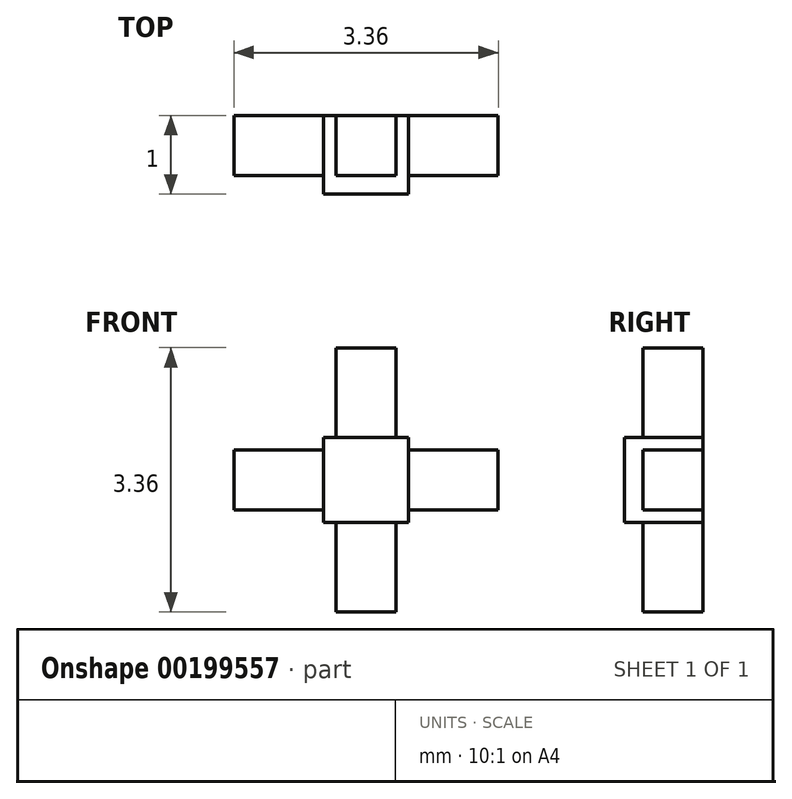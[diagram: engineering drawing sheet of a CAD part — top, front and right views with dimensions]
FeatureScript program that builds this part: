
annotation { "Feature Type Name" : "Feature", "Feature Type Description" : "" }
export const myFeature = defineFeature(function(context is Context, id is Id, definition is map)
    precondition{}
    {
        {
            var Q0;
            Q0=qCreatedBy(makeId("Front.planeOp"),FACE);
            var sketch = newSketch(context, id + "F0", { "sketchPlane" : qUnion([Q0])});
            skLineSegment(sketch, "E0.bottom", {"start": v(0.54, 0.54) * mm, "end": v(-0.54, 0.54) * mm});
            skLineSegment(sketch, "E0.top", {"start": v(0.54, -0.54) * mm, "end": v(-0.54, -0.54) * mm});
            skLineSegment(sketch, "E0.left", {"start": v(0.54, 0.54) * mm, "end": v(0.54, -0.54) * mm});
            skLineSegment(sketch, "E0.right", {"start": v(-0.54, 0.54) * mm, "end": v(-0.54, -0.54) * mm});
            skPoint(sketch, "E0.middle", {"position": v(0, 0) * mm});
            skSolve(sketch);
        }
        {
            var Q0;
            Q0 = qSketchRegion(id + "F0", true);
            extrude(context, id + "F1", {"entities" : qUnion([Q0]), "depth" : 1 * mm});
        }
        {
            var Q0;
            Q0=makeQuery(id+"F1.opExtrude","SWEPT_FACE",FACE,{"disambiguationData":[OSD([sQuery(id+"F0.wireOp",EDGE,"E0.top")])]});
            var sketch = newSketch(context, id + "F2", { "sketchPlane" : qUnion([Q0])});
            skLineSegment(sketch, "E1", {"start": v(-0.54, 0) * mm, "end": v(-0.38, 0) * mm});
            skLineSegment(sketch, "E2.bottom", {"start": v(-0.38, 0) * mm, "end": v(0.38, 0) * mm});
            skLineSegment(sketch, "E2.top", {"start": v(-0.38, 0.76) * mm, "end": v(0.38, 0.76) * mm});
            skLineSegment(sketch, "E2.left", {"start": v(-0.38, 0) * mm, "end": v(-0.38, 0.76) * mm});
            skLineSegment(sketch, "E2.right", {"start": v(0.38, 0) * mm, "end": v(0.38, 0.76) * mm});
            skSolve(sketch);
        }
        {
            var Q0;
            Q0 = qSketchRegion(id + "F2", true);
            extrude(context, id + "F3", {"entities" : qUnion([Q0]), "operationType" : NewBodyOperationType.ADD, "depth" : 1.14 * mm});
        }
        {
            var Q0;
            Q0=makeQuery(id+"F1.opExtrude","SWEPT_FACE",FACE,{"disambiguationData":[OSD([sQuery(id+"F0.wireOp",EDGE,"E0.right")])]});
            var sketch = newSketch(context, id + "F4", { "sketchPlane" : qUnion([Q0])});
            skLineSegment(sketch, "E3", {"start": v(0, 0.54) * mm, "end": v(0, 0.38) * mm});
            skLineSegment(sketch, "E4.bottom", {"start": v(0, 0.38) * mm, "end": v(0.76, 0.38) * mm});
            skLineSegment(sketch, "E4.top", {"start": v(0, -0.38) * mm, "end": v(0.76, -0.38) * mm});
            skLineSegment(sketch, "E4.left", {"start": v(0, 0.38) * mm, "end": v(0, -0.38) * mm});
            skLineSegment(sketch, "E4.right", {"start": v(0.76, 0.38) * mm, "end": v(0.76, -0.38) * mm});
            skSolve(sketch);
        }
        {
            var Q0;
            Q0 = qSketchRegion(id + "F4", true);
            extrude(context, id + "F5", {"entities" : qUnion([Q0]), "operationType" : NewBodyOperationType.ADD, "depth" : 1.14 * mm});
        }
        {
            var Q0;
            Q0=makeQuery(id+"F1.opExtrude","SWEPT_FACE",FACE,{"disambiguationData":[OSD([sQuery(id+"F0.wireOp",EDGE,"E0.bottom")])]});
            var sketch = newSketch(context, id + "F6", { "sketchPlane" : qUnion([Q0])});
            skLineSegment(sketch, "E5", {"start": v(0.54, 0) * mm, "end": v(0.38, 0) * mm});
            skLineSegment(sketch, "E6.bottom", {"start": v(0.38, 0) * mm, "end": v(-0.38, 0) * mm});
            skLineSegment(sketch, "E6.top", {"start": v(0.38, -0.76) * mm, "end": v(-0.38, -0.76) * mm});
            skLineSegment(sketch, "E6.left", {"start": v(0.38, 0) * mm, "end": v(0.38, -0.76) * mm});
            skLineSegment(sketch, "E6.right", {"start": v(-0.38, 0) * mm, "end": v(-0.38, -0.76) * mm});
            skSolve(sketch);
        }
        {
            var Q0;
            Q0 = qSketchRegion(id + "F6", true);
            extrude(context, id + "F7", {"entities" : qUnion([Q0]), "operationType" : NewBodyOperationType.ADD, "depth" : 1.14 * mm});
        }
        {
            var Q0;
            Q0=makeQuery(id+"F1.opExtrude","SWEPT_FACE",FACE,{"disambiguationData":[OSD([sQuery(id+"F0.wireOp",EDGE,"E0.left")])]});
            var sketch = newSketch(context, id + "F8", { "sketchPlane" : qUnion([Q0])});
            skLineSegment(sketch, "E7", {"start": v(0, -0.54) * mm, "end": v(0, -0.38) * mm});
            skLineSegment(sketch, "E8.bottom", {"start": v(0, -0.38) * mm, "end": v(-0.76, -0.38) * mm});
            skLineSegment(sketch, "E8.top", {"start": v(0, 0.38) * mm, "end": v(-0.76, 0.38) * mm});
            skLineSegment(sketch, "E8.left", {"start": v(0, -0.38) * mm, "end": v(0, 0.38) * mm});
            skLineSegment(sketch, "E8.right", {"start": v(-0.76, -0.38) * mm, "end": v(-0.76, 0.38) * mm});
            skSolve(sketch);
        }
        {
            var Q0;
            Q0 = qSketchRegion(id + "F8", true);
            extrude(context, id + "F9", {"entities" : qUnion([Q0]), "operationType" : NewBodyOperationType.ADD, "depth" : 1.14 * mm});
        }
    });
